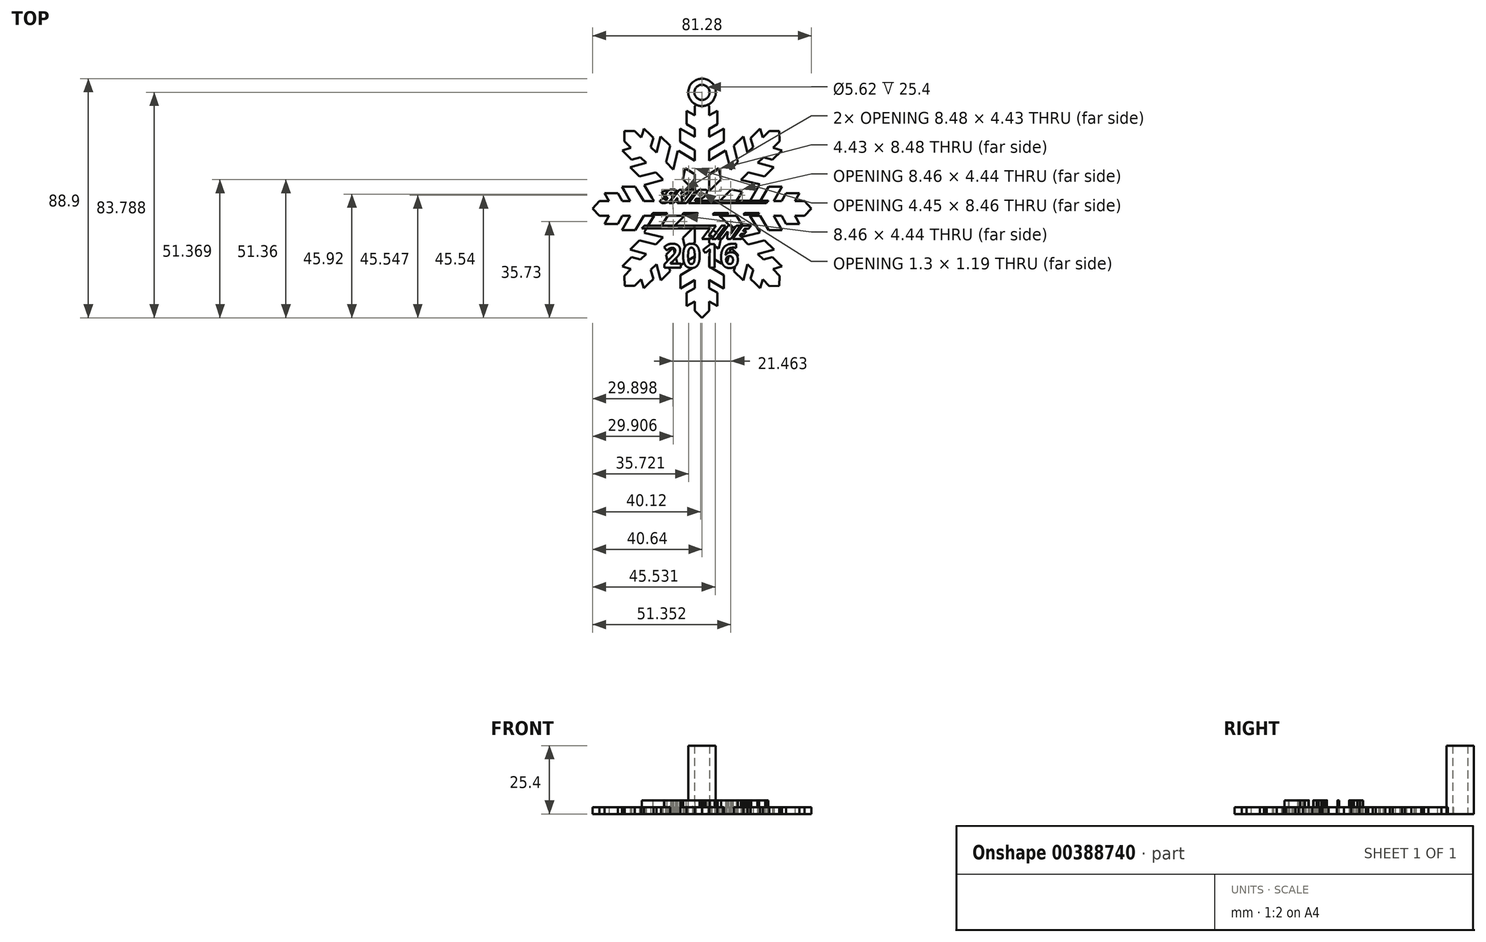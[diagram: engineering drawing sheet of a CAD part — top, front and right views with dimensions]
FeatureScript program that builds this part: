
annotation { "Feature Type Name" : "Feature", "Feature Type Description" : "" }
export const myFeature = defineFeature(function(context is Context, id is Id, definition is map)
    precondition{}
    {
        {
            var Q0;
            Q0=qCreatedBy(makeId("Top.planeOp"),FACE);
            var sketch = newSketch(context, id + "F0", { "sketchPlane" : qUnion([Q0])});
            skFitSpline(sketch, "E0", {"points": [v(-1.17, 4.88) * mm, v(-0.68, 4.68) * mm, v(0.05, 5.08) * mm, v(0.12, 5.6) * mm]});
            skArc(sketch, "E1", {"start": v(0.12, 5.6) * mm, "mid": v(0.11, 5.67) * mm, "end": v(0.07, 5.73) * mm});
            skFitSpline(sketch, "E2", {"points": [v(0.07, 5.73) * mm, v(-0.05, 5.86) * mm, v(-0.5, 5.81) * mm, v(-0.6, 5.67) * mm]});
            skLineSegment(sketch, "E3", {"start": v(-0.6, 5.67) * mm, "end": v(-1.17, 4.88) * mm});
            skEllipticalArc(sketch, "E4", {});
            skArc(sketch, "E5", {"start": v(15.96, -7.56) * mm, "mid": v(15.87, -7.56) * mm, "end": v(15.8, -7.6) * mm});
            skArc(sketch, "E6", {"start": v(15.8, -7.6) * mm, "mid": v(15.52, -7.98) * mm, "end": v(15.26, -8.37) * mm});
            skLineSegment(sketch, "E7", {"start": v(15.26, -8.37) * mm, "end": v(16.54, -8.4) * mm});
            skArc(sketch, "E8", {"start": v(14.65, -9.46) * mm, "mid": v(14.5, -9.47) * mm, "end": v(14.4, -9.57) * mm});
            skArc(sketch, "E9", {"start": v(14.06, -10.09) * mm, "mid": v(14.23, -9.83) * mm, "end": v(14.4, -9.57) * mm});
            skLineSegment(sketch, "E10", {"start": v(15.39, -10.18) * mm, "end": v(14.62, -11.34) * mm});
            skArc(sketch, "E11", {"start": v(14.5, -11.4) * mm, "mid": v(14.56, -11.38) * mm, "end": v(14.62, -11.34) * mm});
            skLineSegment(sketch, "E12", {"start": v(-9.28, 6.52) * mm, "end": v(-10.53, 5.46) * mm});
            skArc(sketch, "E13", {"start": v(-10.53, 5.46) * mm, "mid": v(-10.74, 5.59) * mm, "end": v(-10.96, 5.7) * mm});
            skArc(sketch, "E14", {"start": v(-10.96, 5.7) * mm, "mid": v(-11.16, 5.75) * mm, "end": v(-11.37, 5.75) * mm});
            skFitSpline(sketch, "E15", {"points": [v(-11.37, 5.75) * mm, v(-11.84, 5.7) * mm, v(-11.92, 5.5) * mm, v(-11.63, 5.14) * mm]});
            skArc(sketch, "E16", {"start": v(-11.63, 5.14) * mm, "mid": v(-11.41, 4.9) * mm, "end": v(-11.19, 4.67) * mm});
            skArc(sketch, "E17", {"start": v(-11.05, 4.4) * mm, "mid": v(-11.1, 4.55) * mm, "end": v(-11.19, 4.67) * mm});
            skArc(sketch, "E18", {"start": v(-11.29, 3.53) * mm, "mid": v(-11.1, 3.95) * mm, "end": v(-11.05, 4.4) * mm});
            skArc(sketch, "E19", {"start": v(-13, 2.22) * mm, "mid": v(-12.04, 2.74) * mm, "end": v(-11.29, 3.53) * mm});
            skArc(sketch, "E20", {"start": v(-14.5, 1.95) * mm, "mid": v(-13.73, 2) * mm, "end": v(-13, 2.22) * mm});
            skArc(sketch, "E21", {"start": v(-15.55, 2.56) * mm, "mid": v(-15.1, 2.13) * mm, "end": v(-14.5, 1.95) * mm});
            skArc(sketch, "E22", {"start": v(-15.5, 2.93) * mm, "mid": v(-15.61, 2.76) * mm, "end": v(-15.55, 2.56) * mm});
            skFitSpline(sketch, "E23", {"points": [v(-13.41, 5.49) * mm, v(-12.78, 6.4) * mm, v(-11.95, 6.98) * mm, v(-10.83, 7.1) * mm]});
            skArc(sketch, "E24", {"start": v(-9.59, 6.78) * mm, "mid": v(-10.18, 7.06) * mm, "end": v(-10.83, 7.1) * mm});
            skArc(sketch, "E25", {"start": v(-9.59, 6.78) * mm, "mid": v(-9.43, 6.65) * mm, "end": v(-9.28, 6.52) * mm});
            skLineSegment(sketch, "E26", {"start": v(15.87, -9.37) * mm, "end": v(16.54, -8.4) * mm});
            skLineSegment(sketch, "E27", {"start": v(14.65, -9.46) * mm, "end": v(15.7, -9.47) * mm});
            skArc(sketch, "E28", {"start": v(15.7, -9.47) * mm, "mid": v(15.8, -9.44) * mm, "end": v(15.87, -9.37) * mm});
            skLineSegment(sketch, "E29", {"start": v(15.39, -10.18) * mm, "end": v(13.99, -10.18) * mm});
            skLineSegment(sketch, "E30", {"start": v(14.06, -10.09) * mm, "end": v(13.99, -10.18) * mm});
            skFitSpline(sketch, "E31", {"points": [v(-2.46, 3.22) * mm, v(-2.3, 3.55) * mm, v(-2.05, 3.64) * mm, v(-1.68, 3.64) * mm]});
            skFitSpline(sketch, "E32", {"points": [v(-1.68, 3.64) * mm, v(-0.53, 3.63) * mm, v(0.45, 4.01) * mm, v(1.2, 4.93) * mm]});
            skFitSpline(sketch, "E33", {"points": [v(1.2, 4.93) * mm, v(1.46, 5.25) * mm, v(1.71, 5.58) * mm, v(1.8, 6) * mm]});
            skFitSpline(sketch, "E34", {"points": [v(1.8, 6) * mm, v(1.88, 6.49) * mm, v(1.65, 6.85) * mm, v(1.16, 6.88) * mm]});
            skArc(sketch, "E35", {"start": v(-18.22, -1.75) * mm, "mid": v(-18.28, -1.76) * mm, "end": v(-18.34, -1.8) * mm});
            skLineSegment(sketch, "E36", {"start": v(-18.34, -1.8) * mm, "end": v(-18.79, -2.39) * mm});
            skLineSegment(sketch, "E37", {"start": v(-18.79, -2.39) * mm, "end": v(-13.62, -2.39) * mm});
            skArc(sketch, "E38", {"start": v(-13.62, -2.39) * mm, "mid": v(-13.55, -2.38) * mm, "end": v(-13.48, -2.35) * mm});
            skArc(sketch, "E39", {"start": v(-13.48, -2.35) * mm, "mid": v(-13.2, -2.05) * mm, "end": v(-12.9, -1.75) * mm});
            skLineSegment(sketch, "E40", {"start": v(-12.9, -1.75) * mm, "end": v(-18.22, -1.75) * mm});
            skArc(sketch, "E41", {"start": v(15.93, -1.74) * mm, "mid": v(15.84, -1.75) * mm, "end": v(15.77, -1.8) * mm});
            skLineSegment(sketch, "E42", {"start": v(15.77, -1.8) * mm, "end": v(15.35, -2.38) * mm});
            skLineSegment(sketch, "E43", {"start": v(15.35, -2.38) * mm, "end": v(20.52, -2.38) * mm});
            skArc(sketch, "E44", {"start": v(20.52, -2.38) * mm, "mid": v(20.57, -2.38) * mm, "end": v(20.62, -2.36) * mm});
            skArc(sketch, "E45", {"start": v(20.62, -2.36) * mm, "mid": v(20.92, -2.05) * mm, "end": v(21.22, -1.74) * mm});
            skLineSegment(sketch, "E46", {"start": v(21.22, -1.74) * mm, "end": v(15.93, -1.74) * mm});
            skArc(sketch, "E47", {"start": v(-5.78, 2.11) * mm, "mid": v(-5.92, 2) * mm, "end": v(-6.1, 1.96) * mm});
            skArc(sketch, "E48", {"start": v(-6.1, 1.96) * mm, "mid": v(-6.72, 1.97) * mm, "end": v(-7.33, 1.97) * mm});
            skArc(sketch, "E49", {"start": v(-7.33, 1.97) * mm, "mid": v(-7.22, 2.12) * mm, "end": v(-7.11, 2.27) * mm});
            skLineSegment(sketch, "E50", {"start": v(-7.11, 2.27) * mm, "end": v(-3.68, 6.81) * mm});
            skArc(sketch, "E51", {"start": v(-3.68, 6.81) * mm, "mid": v(-3.55, 6.93) * mm, "end": v(-3.38, 6.96) * mm});
            skArc(sketch, "E52", {"start": v(-3.38, 6.96) * mm, "mid": v(-2.77, 6.95) * mm, "end": v(-2.17, 6.96) * mm});
            skLineSegment(sketch, "E53", {"start": v(-2.17, 6.96) * mm, "end": v(-3.75, 4.83) * mm});
            skLineSegment(sketch, "E54", {"start": v(-3.75, 4.83) * mm, "end": v(-5.78, 2.11) * mm});
            skArc(sketch, "E55", {"start": v(-7.82, 5.6) * mm, "mid": v(-7.35, 6.25) * mm, "end": v(-6.88, 6.9) * mm});
            skArc(sketch, "E56", {"start": v(-6.88, 6.9) * mm, "mid": v(-6.96, 6.91) * mm, "end": v(-7.05, 6.93) * mm});
            skArc(sketch, "E57", {"start": v(-7.05, 6.93) * mm, "mid": v(-7.61, 6.93) * mm, "end": v(-8.17, 6.93) * mm});
            skArc(sketch, "E58", {"start": v(-8.17, 6.93) * mm, "mid": v(-8.37, 6.9) * mm, "end": v(-8.52, 6.78) * mm});
            skLineSegment(sketch, "E59", {"start": v(-8.52, 6.78) * mm, "end": v(-11.44, 3.01) * mm});
            skArc(sketch, "E60", {"start": v(-11.44, 3.01) * mm, "mid": v(-11.82, 2.52) * mm, "end": v(-12.21, 2.03) * mm});
            skArc(sketch, "E61", {"start": v(-12.21, 2.03) * mm, "mid": v(-12.06, 2.01) * mm, "end": v(-11.9, 2) * mm});
            skArc(sketch, "E62", {"start": v(-11.9, 2) * mm, "mid": v(-11.36, 2) * mm, "end": v(-10.83, 1.99) * mm});
            skArc(sketch, "E63", {"start": v(-10.83, 1.99) * mm, "mid": v(-10.66, 2) * mm, "end": v(-10.54, 2.12) * mm});
            skLineSegment(sketch, "E64", {"start": v(-10.54, 2.12) * mm, "end": v(-9.3, 3.76) * mm});
            skArc(sketch, "E65", {"start": v(-9.3, 3.76) * mm, "mid": v(-9.26, 3.8) * mm, "end": v(-9.22, 3.84) * mm});
            skLineSegment(sketch, "E66", {"start": v(-9.22, 3.84) * mm, "end": v(-9.16, 3.83) * mm});
            skLineSegment(sketch, "E67", {"start": v(-9.16, 3.83) * mm, "end": v(-9.16, 1.97) * mm});
            skLineSegment(sketch, "E68", {"start": v(-9.16, 1.97) * mm, "end": v(-7.34, 1.97) * mm});
            skLineSegment(sketch, "E69", {"start": v(-7.34, 1.97) * mm, "end": v(-7.5, 4.24) * mm});
            skArc(sketch, "E70", {"start": v(-7.5, 4.24) * mm, "mid": v(-7.46, 4.5) * mm, "end": v(-7.27, 4.67) * mm});
            skLineSegment(sketch, "E71", {"start": v(-7.27, 4.67) * mm, "end": v(-4.03, 6.74) * mm});
            skArc(sketch, "E72", {"start": v(-4.03, 6.74) * mm, "mid": v(-3.9, 6.86) * mm, "end": v(-3.76, 6.98) * mm});
            skLineSegment(sketch, "E73", {"start": v(-3.76, 6.98) * mm, "end": v(-5.75, 6.98) * mm});
            skArc(sketch, "E74", {"start": v(-5.75, 6.98) * mm, "mid": v(-5.84, 6.96) * mm, "end": v(-5.92, 6.91) * mm});
            skLineSegment(sketch, "E75", {"start": v(-5.92, 6.91) * mm, "end": v(-6.93, 6.2) * mm});
            skLineSegment(sketch, "E76", {"start": v(-6.93, 6.2) * mm, "end": v(-7.8, 5.58) * mm});
            skArc(sketch, "E77", {"start": v(-7.8, 5.58) * mm, "mid": v(-7.82, 5.6) * mm, "end": v(-7.82, 5.6) * mm});
            skLineSegment(sketch, "E78", {"start": v(-15.5, 2.93) * mm, "end": v(-14.4, 3.86) * mm});
            skArc(sketch, "E79", {"start": v(-14.4, 3.86) * mm, "mid": v(-14.2, 3.67) * mm, "end": v(-14, 3.5) * mm});
            skArc(sketch, "E80", {"start": v(-14, 3.5) * mm, "mid": v(-13.48, 3.3) * mm, "end": v(-12.97, 3.5) * mm});
            skArc(sketch, "E81", {"start": v(-12.97, 3.5) * mm, "mid": v(-12.85, 3.68) * mm, "end": v(-12.88, 3.9) * mm});
            skArc(sketch, "E82", {"start": v(-12.88, 3.9) * mm, "mid": v(-13.13, 4.24) * mm, "end": v(-13.41, 4.55) * mm});
            skArc(sketch, "E83", {"start": v(-13.41, 4.55) * mm, "mid": v(-13.58, 4.8) * mm, "end": v(-13.58, 5.1) * mm});
            skArc(sketch, "E84", {"start": v(-13.58, 5.1) * mm, "mid": v(-13.51, 5.3) * mm, "end": v(-13.41, 5.49) * mm});
            skLineSegment(sketch, "E85", {"start": v(2.96, -11.36) * mm, "end": v(0.03, -11.36) * mm});
            skLineSegment(sketch, "E86", {"start": v(0.03, -11.36) * mm, "end": v(2.93, -7.41) * mm});
            skLineSegment(sketch, "E87", {"start": v(2.93, -7.41) * mm, "end": v(-22.35, -7.41) * mm});
            skArc(sketch, "E88", {"start": v(-22.35, -7.41) * mm, "mid": v(-21.88, -6.88) * mm, "end": v(-21.4, -6.36) * mm});
            skLineSegment(sketch, "E89", {"start": v(-21.4, -6.36) * mm, "end": v(5.26, -6.38) * mm});
            skLineSegment(sketch, "E90", {"start": v(5.26, -6.38) * mm, "end": v(2.48, -10.16) * mm});
            skArc(sketch, "E91", {"start": v(2.48, -10.16) * mm, "mid": v(3.16, -10.16) * mm, "end": v(3.85, -10.17) * mm});
            skArc(sketch, "E92", {"start": v(3.85, -10.17) * mm, "mid": v(3.47, -10.74) * mm, "end": v(3.08, -11.32) * mm});
            skArc(sketch, "E93", {"start": v(3.08, -11.32) * mm, "mid": v(3.02, -11.35) * mm, "end": v(2.96, -11.36) * mm});
            skArc(sketch, "E94", {"start": v(7.46, -6.36) * mm, "mid": v(7.32, -6.39) * mm, "end": v(7.21, -6.48) * mm});
            skLineSegment(sketch, "E95", {"start": v(7.21, -6.48) * mm, "end": v(3.73, -11.26) * mm});
            skArc(sketch, "E96", {"start": v(3.73, -11.26) * mm, "mid": v(3.69, -11.33) * mm, "end": v(3.66, -11.4) * mm});
            skLineSegment(sketch, "E97", {"start": v(3.66, -11.4) * mm, "end": v(5, -11.4) * mm});
            skArc(sketch, "E98", {"start": v(5, -11.4) * mm, "mid": v(5.1, -11.37) * mm, "end": v(5.17, -11.3) * mm});
            skArc(sketch, "E99", {"start": v(5.17, -11.3) * mm, "mid": v(5.52, -10.83) * mm, "end": v(5.87, -10.36) * mm});
            skLineSegment(sketch, "E100", {"start": v(5.87, -10.36) * mm, "end": v(8.74, -6.42) * mm});
            skLineSegment(sketch, "E101", {"start": v(8.74, -6.42) * mm, "end": v(8.73, -6.36) * mm});
            skLineSegment(sketch, "E102", {"start": v(8.73, -6.36) * mm, "end": v(7.46, -6.36) * mm});
            skLineSegment(sketch, "E103", {"start": v(10.81, -9.31) * mm, "end": v(12.68, -6.56) * mm});
            skArc(sketch, "E104", {"start": v(12.68, -6.56) * mm, "mid": v(12.84, -6.43) * mm, "end": v(13.03, -6.36) * mm});
            skArc(sketch, "E105", {"start": v(13.03, -6.36) * mm, "mid": v(13.65, -6.36) * mm, "end": v(14.26, -6.37) * mm});
            skArc(sketch, "E106", {"start": v(14.26, -6.37) * mm, "mid": v(14.2, -6.45) * mm, "end": v(14.14, -6.54) * mm});
            skLineSegment(sketch, "E107", {"start": v(14.14, -6.54) * mm, "end": v(10.76, -11.26) * mm});
            skArc(sketch, "E108", {"start": v(10.76, -11.26) * mm, "mid": v(10.64, -11.37) * mm, "end": v(10.49, -11.4) * mm});
            skArc(sketch, "E109", {"start": v(10.49, -11.4) * mm, "mid": v(9.95, -11.39) * mm, "end": v(9.4, -11.39) * mm});
            skLineSegment(sketch, "E110", {"start": v(9.4, -11.39) * mm, "end": v(9.52, -8.57) * mm});
            skLineSegment(sketch, "E111", {"start": v(9.52, -8.57) * mm, "end": v(7.54, -11.25) * mm});
            skArc(sketch, "E112", {"start": v(7.54, -11.25) * mm, "mid": v(7.4, -11.35) * mm, "end": v(7.24, -11.38) * mm});
            skArc(sketch, "E113", {"start": v(7.24, -11.38) * mm, "mid": v(6.56, -11.38) * mm, "end": v(5.89, -11.38) * mm});
            skArc(sketch, "E114", {"start": v(5.89, -11.38) * mm, "mid": v(5.96, -11.28) * mm, "end": v(6.03, -11.17) * mm});
            skLineSegment(sketch, "E115", {"start": v(6.03, -11.17) * mm, "end": v(9.6, -6.48) * mm});
            skArc(sketch, "E116", {"start": v(9.6, -6.48) * mm, "mid": v(9.74, -6.35) * mm, "end": v(9.91, -6.32) * mm});
            skArc(sketch, "E117", {"start": v(9.91, -6.32) * mm, "mid": v(10.45, -6.33) * mm, "end": v(11, -6.33) * mm});
            skLineSegment(sketch, "E118", {"start": v(11, -6.33) * mm, "end": v(10.78, -9.3) * mm});
            skLineSegment(sketch, "E119", {"start": v(14.5, -11.4) * mm, "end": v(11.59, -11.38) * mm});
            skLineSegment(sketch, "E120", {"start": v(11.59, -11.38) * mm, "end": v(11.44, -11.35) * mm});
            skLineSegment(sketch, "E121", {"start": v(11.44, -11.35) * mm, "end": v(12.5, -9.88) * mm});
            skLineSegment(sketch, "E122", {"start": v(12.5, -9.88) * mm, "end": v(14.94, -6.53) * mm});
            skArc(sketch, "E123", {"start": v(14.94, -6.53) * mm, "mid": v(15.06, -6.42) * mm, "end": v(15.21, -6.39) * mm});
            skLineSegment(sketch, "E124", {"start": v(15.21, -6.39) * mm, "end": v(18.1, -6.36) * mm});
            skArc(sketch, "E125", {"start": v(18.1, -6.36) * mm, "mid": v(18.18, -6.36) * mm, "end": v(18.26, -6.37) * mm});
            skArc(sketch, "E126", {"start": v(18.26, -6.37) * mm, "mid": v(18.1, -6.57) * mm, "end": v(17.92, -6.77) * mm});
            skArc(sketch, "E127", {"start": v(17.92, -6.77) * mm, "mid": v(17.62, -7.14) * mm, "end": v(17.31, -7.5) * mm});
            skArc(sketch, "E128", {"start": v(17.31, -7.5) * mm, "mid": v(17.2, -7.55) * mm, "end": v(17.1, -7.56) * mm});
            skArc(sketch, "E129", {"start": v(17.1, -7.56) * mm, "mid": v(16.53, -7.56) * mm, "end": v(15.96, -7.56) * mm});
            skArc(sketch, "E130", {"start": v(-2.7, 2.87) * mm, "mid": v(-2.57, 3.04) * mm, "end": v(-2.46, 3.22) * mm});
            skLineSegment(sketch, "E131", {"start": v(-2.7, 2.87) * mm, "end": v(24.62, 2.87) * mm});
            skArc(sketch, "E132", {"start": v(24.64, 2.8) * mm, "mid": v(24.38, 2.54) * mm, "end": v(24.14, 2.26) * mm});
            skArc(sketch, "E133", {"start": v(23.53, 1.99) * mm, "mid": v(23.87, 2.04) * mm, "end": v(24.14, 2.26) * mm});
            skLineSegment(sketch, "E134", {"start": v(23.53, 1.99) * mm, "end": v(6.56, 1.99) * mm});
            skLineSegment(sketch, "E135", {"start": v(6.56, 1.99) * mm, "end": v(6.54, 1.99) * mm});
            skLineSegment(sketch, "E136", {"start": v(6.54, 1.99) * mm, "end": v(-4.65, 1.98) * mm});
            skLineSegment(sketch, "E137", {"start": v(-4.65, 1.98) * mm, "end": v(-4.9, 1.98) * mm});
            skArc(sketch, "E138", {"start": v(-4.8, 2.14) * mm, "mid": v(-4.85, 2.06) * mm, "end": v(-4.9, 1.98) * mm});
            skLineSegment(sketch, "E139", {"start": v(-4.8, 2.14) * mm, "end": v(-1.22, 6.8) * mm});
            skArc(sketch, "E140", {"start": v(-0.9, 6.97) * mm, "mid": v(-1.08, 6.94) * mm, "end": v(-1.22, 6.8) * mm});
            skArc(sketch, "E141", {"start": v(1.16, 6.88) * mm, "mid": v(0.14, 6.94) * mm, "end": v(-0.9, 6.97) * mm});
            skLineSegment(sketch, "E142", {"start": v(24.64, 2.8) * mm, "end": v(24.62, 2.87) * mm});
            skLineSegment(sketch, "E143", {"start": v(-6.82, -1.75) * mm, "end": v(-1.61, -1.75) * mm});
            skArc(sketch, "E144", {"start": v(-2.1, -2.34) * mm, "mid": v(-1.83, -2.06) * mm, "end": v(-1.56, -1.78) * mm});
            skArc(sketch, "E145", {"start": v(-2.23, -2.37) * mm, "mid": v(-2.17, -2.37) * mm, "end": v(-2.1, -2.34) * mm});
            skLineSegment(sketch, "E146", {"start": v(-2.23, -2.37) * mm, "end": v(-7.43, -2.37) * mm});
            skLineSegment(sketch, "E147", {"start": v(-7.43, -2.37) * mm, "end": v(-6.98, -1.81) * mm});
            skArc(sketch, "E148", {"start": v(-6.82, -1.75) * mm, "mid": v(-6.9, -1.77) * mm, "end": v(-6.98, -1.81) * mm});
            skLineSegment(sketch, "E149", {"start": v(-1.56, -1.78) * mm, "end": v(-1.61, -1.75) * mm});
            skArc(sketch, "E150", {"start": v(4.52, -1.76) * mm, "mid": v(4.44, -1.78) * mm, "end": v(4.37, -1.82) * mm});
            skLineSegment(sketch, "E151", {"start": v(4.37, -1.82) * mm, "end": v(3.92, -2.38) * mm});
            skLineSegment(sketch, "E152", {"start": v(3.92, -2.38) * mm, "end": v(9.11, -2.38) * mm});
            skArc(sketch, "E153", {"start": v(9.11, -2.38) * mm, "mid": v(9.18, -2.38) * mm, "end": v(9.24, -2.35) * mm});
            skArc(sketch, "E154", {"start": v(9.79, -1.79) * mm, "mid": v(9.5, -2.07) * mm, "end": v(9.24, -2.35) * mm});
            skLineSegment(sketch, "E155", {"start": v(9.73, -1.76) * mm, "end": v(4.52, -1.76) * mm});
            skLineSegment(sketch, "E156", {"start": v(9.79, -1.79) * mm, "end": v(9.73, -1.76) * mm});
            const initialGuessF0  = {"E4": [0.010823041612434577, -0.009243857390442117, 0.9870975910491284, -0.16011978561379503, 6.825542101971352e-05, 6.825542101971352e-05, 4.110214, 4.709019]};
            skSetInitialGuess(sketch, initialGuessF0);
            skSolve(sketch);
        }
        {
            var Q0;
            Q0 = qSketchRegion(id + "F0", true);
            extrude(context, id + "F1", {"entities" : qUnion([Q0]), "depth" : 5.08 * mm});
        }
        {
            var Q0;
            Q0=qCreatedBy(makeId("Top.planeOp"),FACE);
            var sketch = newSketch(context, id + "F2", { "sketchPlane" : qUnion([Q0])});
            skLineSegment(sketch, "E157", {"start": v(40.64, -0.01) * mm, "end": v(40.63, 0) * mm});
            skLineSegment(sketch, "E158", {"start": v(40.63, 0) * mm, "end": v(38.05, 2.69) * mm});
            skLineSegment(sketch, "E159", {"start": v(38.05, 2.69) * mm, "end": v(34.6, 2.69) * mm});
            skLineSegment(sketch, "E160", {"start": v(34.6, 2.69) * mm, "end": v(36.21, 5.73) * mm});
            skLineSegment(sketch, "E161", {"start": v(36.21, 5.73) * mm, "end": v(31.28, 5.73) * mm});
            skLineSegment(sketch, "E162", {"start": v(31.28, 5.73) * mm, "end": v(29.58, 2.69) * mm});
            skLineSegment(sketch, "E163", {"start": v(29.58, 2.69) * mm, "end": v(26.63, 2.69) * mm});
            skLineSegment(sketch, "E164", {"start": v(26.63, 2.69) * mm, "end": v(29.72, 8.08) * mm});
            skLineSegment(sketch, "E165", {"start": v(29.72, 8.08) * mm, "end": v(24.8, 8.08) * mm});
            skLineSegment(sketch, "E166", {"start": v(24.8, 8.08) * mm, "end": v(21.6, 2.69) * mm});
            skLineSegment(sketch, "E167", {"start": v(21.6, 2.69) * mm, "end": v(17.77, 2.69) * mm});
            skLineSegment(sketch, "E168", {"start": v(17.77, 2.69) * mm, "end": v(20.93, 8.17) * mm});
            skLineSegment(sketch, "E169", {"start": v(20.93, 8.17) * mm, "end": v(21.42, 9.02) * mm});
            skLineSegment(sketch, "E170", {"start": v(21.42, 9.02) * mm, "end": v(14.47, 10.68) * mm});
            skLineSegment(sketch, "E171", {"start": v(14.47, 10.68) * mm, "end": v(16.73, 12.94) * mm});
            skLineSegment(sketch, "E172", {"start": v(16.73, 12.94) * mm, "end": v(17.18, 13.39) * mm});
            skLineSegment(sketch, "E173", {"start": v(17.18, 13.39) * mm, "end": v(23.25, 11.84) * mm});
            skLineSegment(sketch, "E174", {"start": v(23.25, 11.84) * mm, "end": v(26.72, 15.32) * mm});
            skLineSegment(sketch, "E175", {"start": v(26.72, 15.32) * mm, "end": v(20.73, 16.95) * mm});
            skLineSegment(sketch, "E176", {"start": v(20.73, 16.95) * mm, "end": v(22.81, 19.03) * mm});
            skLineSegment(sketch, "E177", {"start": v(22.81, 19.03) * mm, "end": v(26.18, 18.08) * mm});
            skLineSegment(sketch, "E178", {"start": v(26.18, 18.08) * mm, "end": v(29.66, 21.56) * mm});
            skLineSegment(sketch, "E179", {"start": v(29.66, 21.56) * mm, "end": v(26.36, 22.56) * mm});
            skLineSegment(sketch, "E180", {"start": v(26.36, 22.56) * mm, "end": v(28.8, 25) * mm});
            skLineSegment(sketch, "E181", {"start": v(28.8, 25) * mm, "end": v(28.73, 28.74) * mm});
            skLineSegment(sketch, "E182", {"start": v(28.73, 28.74) * mm, "end": v(25, 28.8) * mm});
            skLineSegment(sketch, "E183", {"start": v(25, 28.8) * mm, "end": v(22.56, 26.36) * mm});
            skLineSegment(sketch, "E184", {"start": v(22.56, 26.36) * mm, "end": v(21.55, 29.66) * mm});
            skLineSegment(sketch, "E185", {"start": v(21.55, 29.66) * mm, "end": v(18.07, 26.18) * mm});
            skLineSegment(sketch, "E186", {"start": v(18.07, 26.18) * mm, "end": v(19.02, 22.82) * mm});
            skLineSegment(sketch, "E187", {"start": v(19.02, 22.82) * mm, "end": v(16.93, 20.74) * mm});
            skLineSegment(sketch, "E188", {"start": v(16.93, 20.74) * mm, "end": v(15.3, 26.74) * mm});
            skLineSegment(sketch, "E189", {"start": v(15.3, 26.74) * mm, "end": v(11.83, 23.26) * mm});
            skLineSegment(sketch, "E190", {"start": v(11.83, 23.26) * mm, "end": v(13.38, 17.19) * mm});
            skLineSegment(sketch, "E191", {"start": v(13.38, 17.19) * mm, "end": v(10.67, 14.47) * mm});
            skLineSegment(sketch, "E192", {"start": v(10.67, 14.47) * mm, "end": v(8.78, 21.53) * mm});
            skLineSegment(sketch, "E193", {"start": v(8.78, 21.53) * mm, "end": v(3.94, 18.56) * mm});
            skLineSegment(sketch, "E194", {"start": v(3.94, 18.56) * mm, "end": v(2.68, 17.8) * mm});
            skLineSegment(sketch, "E195", {"start": v(2.68, 17.8) * mm, "end": v(2.68, 21.62) * mm});
            skLineSegment(sketch, "E196", {"start": v(2.68, 21.62) * mm, "end": v(8.07, 24.82) * mm});
            skLineSegment(sketch, "E197", {"start": v(8.07, 24.82) * mm, "end": v(8.07, 29.74) * mm});
            skLineSegment(sketch, "E198", {"start": v(8.07, 29.74) * mm, "end": v(2.68, 26.64) * mm});
            skLineSegment(sketch, "E199", {"start": v(2.68, 26.64) * mm, "end": v(2.68, 29.6) * mm});
            skLineSegment(sketch, "E200", {"start": v(2.68, 29.6) * mm, "end": v(5.72, 31.3) * mm});
            skLineSegment(sketch, "E201", {"start": v(5.72, 31.3) * mm, "end": v(5.72, 36.22) * mm});
            skLineSegment(sketch, "E202", {"start": v(5.72, 36.22) * mm, "end": v(2.68, 34.6) * mm});
            skLineSegment(sketch, "E203", {"start": v(2.68, 34.6) * mm, "end": v(2.68, 38.05) * mm});
            skLineSegment(sketch, "E204", {"start": v(2.68, 38.05) * mm, "end": v(0, 40.64) * mm});
            skLineSegment(sketch, "E205", {"start": v(0, 40.64) * mm, "end": v(-2.69, 38.05) * mm});
            skLineSegment(sketch, "E206", {"start": v(-2.69, 38.05) * mm, "end": v(-2.69, 34.6) * mm});
            skLineSegment(sketch, "E207", {"start": v(-2.69, 34.6) * mm, "end": v(-5.73, 36.22) * mm});
            skLineSegment(sketch, "E208", {"start": v(-5.73, 36.22) * mm, "end": v(-5.73, 34.8) * mm});
            skLineSegment(sketch, "E209", {"start": v(-5.73, 34.8) * mm, "end": v(-5.73, 31.3) * mm});
            skLineSegment(sketch, "E210", {"start": v(-5.73, 31.3) * mm, "end": v(-2.69, 29.6) * mm});
            skLineSegment(sketch, "E211", {"start": v(-2.69, 29.6) * mm, "end": v(-2.69, 26.64) * mm});
            skLineSegment(sketch, "E212", {"start": v(-2.69, 26.64) * mm, "end": v(-8.08, 29.74) * mm});
            skLineSegment(sketch, "E213", {"start": v(-8.08, 29.74) * mm, "end": v(-8.08, 24.82) * mm});
            skLineSegment(sketch, "E214", {"start": v(-8.08, 24.82) * mm, "end": v(-4.29, 22.57) * mm});
            skLineSegment(sketch, "E215", {"start": v(-4.29, 22.57) * mm, "end": v(-2.68, 21.62) * mm});
            skLineSegment(sketch, "E216", {"start": v(-2.68, 21.62) * mm, "end": v(-2.68, 17.78) * mm});
            skLineSegment(sketch, "E217", {"start": v(-2.68, 17.78) * mm, "end": v(-8.62, 21.37) * mm});
            skLineSegment(sketch, "E218", {"start": v(-8.62, 21.37) * mm, "end": v(-8.66, 21.22) * mm});
            skLineSegment(sketch, "E219", {"start": v(-8.66, 21.22) * mm, "end": v(-9.01, 21.43) * mm});
            skLineSegment(sketch, "E220", {"start": v(-9.01, 21.43) * mm, "end": v(-10.68, 14.48) * mm});
            skLineSegment(sketch, "E221", {"start": v(-10.68, 14.48) * mm, "end": v(-10.68, 14.48) * mm});
            skLineSegment(sketch, "E222", {"start": v(-10.68, 14.48) * mm, "end": v(-13.39, 17.2) * mm});
            skLineSegment(sketch, "E223", {"start": v(-13.39, 17.2) * mm, "end": v(-11.84, 23.26) * mm});
            skLineSegment(sketch, "E224", {"start": v(-11.84, 23.26) * mm, "end": v(-15.31, 26.74) * mm});
            skLineSegment(sketch, "E225", {"start": v(-15.31, 26.74) * mm, "end": v(-16.94, 20.74) * mm});
            skLineSegment(sketch, "E226", {"start": v(-16.94, 20.74) * mm, "end": v(-19.02, 22.82) * mm});
            skLineSegment(sketch, "E227", {"start": v(-19.02, 22.82) * mm, "end": v(-18.08, 26.18) * mm});
            skLineSegment(sketch, "E228", {"start": v(-18.08, 26.18) * mm, "end": v(-19.24, 27.34) * mm});
            skLineSegment(sketch, "E229", {"start": v(-19.24, 27.34) * mm, "end": v(-21.56, 29.66) * mm});
            skLineSegment(sketch, "E230", {"start": v(-21.56, 29.66) * mm, "end": v(-22.04, 28.1) * mm});
            skLineSegment(sketch, "E231", {"start": v(-22.04, 28.1) * mm, "end": v(-22.56, 26.36) * mm});
            skLineSegment(sketch, "E232", {"start": v(-22.56, 26.36) * mm, "end": v(-25.01, 28.8) * mm});
            skLineSegment(sketch, "E233", {"start": v(-25.01, 28.8) * mm, "end": v(-28.78, 28.73) * mm});
            skLineSegment(sketch, "E234", {"start": v(-28.78, 28.73) * mm, "end": v(-28.8, 25.9) * mm});
            skLineSegment(sketch, "E235", {"start": v(-28.8, 25.9) * mm, "end": v(-28.8, 25) * mm});
            skLineSegment(sketch, "E236", {"start": v(-28.8, 25) * mm, "end": v(-26.37, 22.56) * mm});
            skLineSegment(sketch, "E237", {"start": v(-26.37, 22.56) * mm, "end": v(-29.66, 21.56) * mm});
            skLineSegment(sketch, "E238", {"start": v(-29.66, 21.56) * mm, "end": v(-26.18, 18.08) * mm});
            skLineSegment(sketch, "E239", {"start": v(-26.18, 18.08) * mm, "end": v(-22.83, 19.02) * mm});
            skLineSegment(sketch, "E240", {"start": v(-22.83, 19.02) * mm, "end": v(-20.74, 16.94) * mm});
            skLineSegment(sketch, "E241", {"start": v(-20.74, 16.94) * mm, "end": v(-26.74, 15.31) * mm});
            skLineSegment(sketch, "E242", {"start": v(-26.74, 15.31) * mm, "end": v(-25.87, 14.45) * mm});
            skLineSegment(sketch, "E243", {"start": v(-25.87, 14.45) * mm, "end": v(-23.26, 11.84) * mm});
            skLineSegment(sketch, "E244", {"start": v(-23.26, 11.84) * mm, "end": v(-17.18, 13.38) * mm});
            skLineSegment(sketch, "E245", {"start": v(-17.18, 13.38) * mm, "end": v(-15.01, 11.22) * mm});
            skLineSegment(sketch, "E246", {"start": v(-15.01, 11.22) * mm, "end": v(-14.47, 10.67) * mm});
            skLineSegment(sketch, "E247", {"start": v(-14.47, 10.67) * mm, "end": v(-21.53, 8.78) * mm});
            skLineSegment(sketch, "E248", {"start": v(-21.53, 8.78) * mm, "end": v(-18.53, 3.89) * mm});
            skLineSegment(sketch, "E249", {"start": v(-18.53, 3.89) * mm, "end": v(-17.8, 2.69) * mm});
            skLineSegment(sketch, "E250", {"start": v(-17.8, 2.69) * mm, "end": v(-20.34, 2.69) * mm});
            skLineSegment(sketch, "E251", {"start": v(-20.34, 2.69) * mm, "end": v(-21.62, 2.69) * mm});
            skLineSegment(sketch, "E252", {"start": v(-21.62, 2.69) * mm, "end": v(-24.24, 7.12) * mm});
            skLineSegment(sketch, "E253", {"start": v(-24.24, 7.12) * mm, "end": v(-24.81, 8.08) * mm});
            skLineSegment(sketch, "E254", {"start": v(-24.81, 8.08) * mm, "end": v(-29.73, 8.08) * mm});
            skLineSegment(sketch, "E255", {"start": v(-29.73, 8.08) * mm, "end": v(-28.86, 6.57) * mm});
            skLineSegment(sketch, "E256", {"start": v(-28.86, 6.57) * mm, "end": v(-26.64, 2.7) * mm});
            skLineSegment(sketch, "E257", {"start": v(-26.64, 2.7) * mm, "end": v(-29.59, 2.7) * mm});
            skLineSegment(sketch, "E258", {"start": v(-29.59, 2.7) * mm, "end": v(-31.3, 5.73) * mm});
            skLineSegment(sketch, "E259", {"start": v(-31.3, 5.73) * mm, "end": v(-36.2, 5.73) * mm});
            skLineSegment(sketch, "E260", {"start": v(-36.2, 5.73) * mm, "end": v(-34.6, 2.7) * mm});
            skLineSegment(sketch, "E261", {"start": v(-34.6, 2.7) * mm, "end": v(-38.05, 2.7) * mm});
            skLineSegment(sketch, "E262", {"start": v(-38.05, 2.7) * mm, "end": v(-40.64, 0) * mm});
            skLineSegment(sketch, "E263", {"start": v(-40.64, 0) * mm, "end": v(-38.05, -2.69) * mm});
            skLineSegment(sketch, "E264", {"start": v(-38.05, -2.69) * mm, "end": v(-34.6, -2.69) * mm});
            skLineSegment(sketch, "E265", {"start": v(-34.6, -2.69) * mm, "end": v(-36.2, -5.72) * mm});
            skLineSegment(sketch, "E266", {"start": v(-36.2, -5.72) * mm, "end": v(-35.5, -5.72) * mm});
            skLineSegment(sketch, "E267", {"start": v(-35.5, -5.72) * mm, "end": v(-31.3, -5.72) * mm});
            skLineSegment(sketch, "E268", {"start": v(-31.3, -5.72) * mm, "end": v(-29.59, -2.69) * mm});
            skLineSegment(sketch, "E269", {"start": v(-29.59, -2.69) * mm, "end": v(-26.64, -2.69) * mm});
            skLineSegment(sketch, "E270", {"start": v(-26.64, -2.69) * mm, "end": v(-29.73, -8.07) * mm});
            skLineSegment(sketch, "E271", {"start": v(-29.73, -8.07) * mm, "end": v(-24.81, -8.07) * mm});
            skLineSegment(sketch, "E272", {"start": v(-24.81, -8.07) * mm, "end": v(-21.62, -2.69) * mm});
            skLineSegment(sketch, "E273", {"start": v(-21.62, -2.69) * mm, "end": v(-17.78, -2.69) * mm});
            skLineSegment(sketch, "E274", {"start": v(-17.78, -2.69) * mm, "end": v(-21.37, -8.6) * mm});
            skLineSegment(sketch, "E275", {"start": v(-21.37, -8.6) * mm, "end": v(-21.22, -8.66) * mm});
            skLineSegment(sketch, "E276", {"start": v(-21.22, -8.66) * mm, "end": v(-21.43, -9.01) * mm});
            skLineSegment(sketch, "E277", {"start": v(-21.43, -9.01) * mm, "end": v(-14.48, -10.68) * mm});
            skLineSegment(sketch, "E278", {"start": v(-14.48, -10.68) * mm, "end": v(-17.18, -13.39) * mm});
            skLineSegment(sketch, "E279", {"start": v(-17.18, -13.39) * mm, "end": v(-23.26, -11.84) * mm});
            skLineSegment(sketch, "E280", {"start": v(-23.26, -11.84) * mm, "end": v(-26.73, -15.3) * mm});
            skLineSegment(sketch, "E281", {"start": v(-26.73, -15.3) * mm, "end": v(-20.74, -16.94) * mm});
            skLineSegment(sketch, "E282", {"start": v(-20.74, -16.94) * mm, "end": v(-22.82, -19.02) * mm});
            skLineSegment(sketch, "E283", {"start": v(-22.82, -19.02) * mm, "end": v(-26.18, -18.08) * mm});
            skLineSegment(sketch, "E284", {"start": v(-26.18, -18.08) * mm, "end": v(-29.66, -21.56) * mm});
            skLineSegment(sketch, "E285", {"start": v(-29.66, -21.56) * mm, "end": v(-26.36, -22.56) * mm});
            skLineSegment(sketch, "E286", {"start": v(-26.36, -22.56) * mm, "end": v(-28.8, -25) * mm});
            skLineSegment(sketch, "E287", {"start": v(-28.8, -25) * mm, "end": v(-28.74, -28.74) * mm});
            skLineSegment(sketch, "E288", {"start": v(-28.74, -28.74) * mm, "end": v(-25.02, -28.8) * mm});
            skLineSegment(sketch, "E289", {"start": v(-25.02, -28.8) * mm, "end": v(-25.01, -28.8) * mm});
            skLineSegment(sketch, "E290", {"start": v(-25.01, -28.8) * mm, "end": v(-22.56, -26.36) * mm});
            skLineSegment(sketch, "E291", {"start": v(-22.56, -26.36) * mm, "end": v(-21.55, -29.66) * mm});
            skLineSegment(sketch, "E292", {"start": v(-21.55, -29.66) * mm, "end": v(-19.82, -27.92) * mm});
            skLineSegment(sketch, "E293", {"start": v(-19.82, -27.92) * mm, "end": v(-18.08, -26.18) * mm});
            skLineSegment(sketch, "E294", {"start": v(-18.08, -26.18) * mm, "end": v(-19.02, -22.82) * mm});
            skLineSegment(sketch, "E295", {"start": v(-19.02, -22.82) * mm, "end": v(-16.93, -20.74) * mm});
            skLineSegment(sketch, "E296", {"start": v(-16.93, -20.74) * mm, "end": v(-15.63, -25.55) * mm});
            skLineSegment(sketch, "E297", {"start": v(-15.63, -25.55) * mm, "end": v(-15.31, -26.74) * mm});
            skLineSegment(sketch, "E298", {"start": v(-15.31, -26.74) * mm, "end": v(-11.83, -23.25) * mm});
            skLineSegment(sketch, "E299", {"start": v(-11.83, -23.25) * mm, "end": v(-13.38, -17.18) * mm});
            skLineSegment(sketch, "E300", {"start": v(-13.38, -17.18) * mm, "end": v(-10.67, -14.46) * mm});
            skLineSegment(sketch, "E301", {"start": v(-10.67, -14.46) * mm, "end": v(-9.01, -21.2) * mm});
            skLineSegment(sketch, "E302", {"start": v(-9.01, -21.2) * mm, "end": v(-8.89, -21.12) * mm});
            skLineSegment(sketch, "E303", {"start": v(-8.89, -21.12) * mm, "end": v(-8.77, -21.52) * mm});
            skLineSegment(sketch, "E304", {"start": v(-8.77, -21.52) * mm, "end": v(-2.69, -17.8) * mm});
            skLineSegment(sketch, "E305", {"start": v(-2.69, -17.8) * mm, "end": v(-2.68, -17.79) * mm});
            skLineSegment(sketch, "E306", {"start": v(-2.68, -17.79) * mm, "end": v(-2.68, -21.61) * mm});
            skLineSegment(sketch, "E307", {"start": v(-2.68, -21.61) * mm, "end": v(-8.07, -24.82) * mm});
            skLineSegment(sketch, "E308", {"start": v(-8.07, -24.82) * mm, "end": v(-8.07, -29.73) * mm});
            skLineSegment(sketch, "E309", {"start": v(-8.07, -29.73) * mm, "end": v(-2.68, -26.64) * mm});
            skLineSegment(sketch, "E310", {"start": v(-2.68, -26.64) * mm, "end": v(-2.68, -29.6) * mm});
            skLineSegment(sketch, "E311", {"start": v(-2.68, -29.6) * mm, "end": v(-5.73, -31.3) * mm});
            skLineSegment(sketch, "E312", {"start": v(-5.73, -31.3) * mm, "end": v(-5.73, -36.22) * mm});
            skLineSegment(sketch, "E313", {"start": v(-5.73, -36.22) * mm, "end": v(-2.68, -34.6) * mm});
            skLineSegment(sketch, "E314", {"start": v(-2.68, -34.6) * mm, "end": v(-2.68, -38.05) * mm});
            skLineSegment(sketch, "E315", {"start": v(-2.68, -38.05) * mm, "end": v(0, -40.64) * mm});
            skLineSegment(sketch, "E316", {"start": v(0, -40.64) * mm, "end": v(2.69, -38.05) * mm});
            skLineSegment(sketch, "E317", {"start": v(2.69, -38.05) * mm, "end": v(2.69, -34.6) * mm});
            skLineSegment(sketch, "E318", {"start": v(2.69, -34.6) * mm, "end": v(5.73, -36.22) * mm});
            skLineSegment(sketch, "E319", {"start": v(5.73, -36.22) * mm, "end": v(5.73, -31.3) * mm});
            skLineSegment(sketch, "E320", {"start": v(5.73, -31.3) * mm, "end": v(2.69, -29.6) * mm});
            skLineSegment(sketch, "E321", {"start": v(2.69, -29.6) * mm, "end": v(2.69, -28.6) * mm});
            skLineSegment(sketch, "E322", {"start": v(2.69, -28.6) * mm, "end": v(2.69, -26.64) * mm});
            skLineSegment(sketch, "E323", {"start": v(2.69, -26.64) * mm, "end": v(7.9, -29.62) * mm});
            skLineSegment(sketch, "E324", {"start": v(7.9, -29.62) * mm, "end": v(8.08, -29.74) * mm});
            skLineSegment(sketch, "E325", {"start": v(8.08, -29.74) * mm, "end": v(8.08, -24.82) * mm});
            skLineSegment(sketch, "E326", {"start": v(8.08, -24.82) * mm, "end": v(2.69, -21.62) * mm});
            skLineSegment(sketch, "E327", {"start": v(2.69, -21.62) * mm, "end": v(2.69, -20.77) * mm});
            skLineSegment(sketch, "E328", {"start": v(2.69, -20.77) * mm, "end": v(2.69, -17.78) * mm});
            skLineSegment(sketch, "E329", {"start": v(2.69, -17.78) * mm, "end": v(7.06, -20.3) * mm});
            skLineSegment(sketch, "E330", {"start": v(7.06, -20.3) * mm, "end": v(9.02, -21.44) * mm});
            skLineSegment(sketch, "E331", {"start": v(9.02, -21.44) * mm, "end": v(10.35, -15.88) * mm});
            skLineSegment(sketch, "E332", {"start": v(10.35, -15.88) * mm, "end": v(10.68, -14.48) * mm});
            skLineSegment(sketch, "E333", {"start": v(10.68, -14.48) * mm, "end": v(13.39, -17.19) * mm});
            skLineSegment(sketch, "E334", {"start": v(13.39, -17.19) * mm, "end": v(11.84, -23.25) * mm});
            skLineSegment(sketch, "E335", {"start": v(11.84, -23.25) * mm, "end": v(15.31, -26.74) * mm});
            skLineSegment(sketch, "E336", {"start": v(15.31, -26.74) * mm, "end": v(16.94, -20.74) * mm});
            skLineSegment(sketch, "E337", {"start": v(16.94, -20.74) * mm, "end": v(18.33, -22.13) * mm});
            skLineSegment(sketch, "E338", {"start": v(18.33, -22.13) * mm, "end": v(19.02, -22.82) * mm});
            skLineSegment(sketch, "E339", {"start": v(19.02, -22.82) * mm, "end": v(18.08, -26.18) * mm});
            skLineSegment(sketch, "E340", {"start": v(18.08, -26.18) * mm, "end": v(19.81, -27.92) * mm});
            skLineSegment(sketch, "E341", {"start": v(19.81, -27.92) * mm, "end": v(21.56, -29.66) * mm});
            skLineSegment(sketch, "E342", {"start": v(21.56, -29.66) * mm, "end": v(22.56, -26.37) * mm});
            skLineSegment(sketch, "E343", {"start": v(22.56, -26.37) * mm, "end": v(25, -28.81) * mm});
            skLineSegment(sketch, "E344", {"start": v(25, -28.81) * mm, "end": v(28.74, -28.74) * mm});
            skLineSegment(sketch, "E345", {"start": v(28.74, -28.74) * mm, "end": v(28.8, -25) * mm});
            skLineSegment(sketch, "E346", {"start": v(28.8, -25) * mm, "end": v(26.37, -22.56) * mm});
            skLineSegment(sketch, "E347", {"start": v(26.37, -22.56) * mm, "end": v(29.66, -21.56) * mm});
            skLineSegment(sketch, "E348", {"start": v(29.66, -21.56) * mm, "end": v(28.62, -20.52) * mm});
            skLineSegment(sketch, "E349", {"start": v(28.62, -20.52) * mm, "end": v(26.18, -18.08) * mm});
            skLineSegment(sketch, "E350", {"start": v(26.18, -18.08) * mm, "end": v(22.82, -19.03) * mm});
            skLineSegment(sketch, "E351", {"start": v(22.82, -19.03) * mm, "end": v(20.74, -16.94) * mm});
            skLineSegment(sketch, "E352", {"start": v(20.74, -16.94) * mm, "end": v(26.73, -15.32) * mm});
            skLineSegment(sketch, "E353", {"start": v(26.73, -15.32) * mm, "end": v(23.26, -11.85) * mm});
            skLineSegment(sketch, "E354", {"start": v(23.26, -11.85) * mm, "end": v(18.28, -13.1) * mm});
            skLineSegment(sketch, "E355", {"start": v(18.28, -13.1) * mm, "end": v(17.18, -13.39) * mm});
            skLineSegment(sketch, "E356", {"start": v(17.18, -13.39) * mm, "end": v(14.47, -10.67) * mm});
            skLineSegment(sketch, "E357", {"start": v(14.47, -10.67) * mm, "end": v(21.2, -9.01) * mm});
            skLineSegment(sketch, "E358", {"start": v(21.2, -9.01) * mm, "end": v(21.13, -8.89) * mm});
            skLineSegment(sketch, "E359", {"start": v(21.13, -8.89) * mm, "end": v(21.53, -8.78) * mm});
            skLineSegment(sketch, "E360", {"start": v(21.53, -8.78) * mm, "end": v(17.79, -2.7) * mm});
            skLineSegment(sketch, "E361", {"start": v(17.79, -2.7) * mm, "end": v(21.62, -2.7) * mm});
            skLineSegment(sketch, "E362", {"start": v(21.62, -2.7) * mm, "end": v(24.4, -7.39) * mm});
            skLineSegment(sketch, "E363", {"start": v(24.4, -7.39) * mm, "end": v(24.81, -8.08) * mm});
            skLineSegment(sketch, "E364", {"start": v(24.81, -8.08) * mm, "end": v(29.73, -8.08) * mm});
            skLineSegment(sketch, "E365", {"start": v(29.73, -8.08) * mm, "end": v(27.3, -3.85) * mm});
            skLineSegment(sketch, "E366", {"start": v(27.3, -3.85) * mm, "end": v(26.64, -2.7) * mm});
            skLineSegment(sketch, "E367", {"start": v(26.64, -2.7) * mm, "end": v(29.59, -2.7) * mm});
            skLineSegment(sketch, "E368", {"start": v(29.59, -2.7) * mm, "end": v(31.3, -5.73) * mm});
            skLineSegment(sketch, "E369", {"start": v(31.3, -5.73) * mm, "end": v(33.75, -5.73) * mm});
            skLineSegment(sketch, "E370", {"start": v(33.75, -5.73) * mm, "end": v(36.22, -5.73) * mm});
            skLineSegment(sketch, "E371", {"start": v(36.22, -5.73) * mm, "end": v(35.07, -3.59) * mm});
            skLineSegment(sketch, "E372", {"start": v(35.07, -3.59) * mm, "end": v(34.6, -2.7) * mm});
            skLineSegment(sketch, "E373", {"start": v(34.6, -2.7) * mm, "end": v(38.05, -2.7) * mm});
            skLineSegment(sketch, "E374", {"start": v(38.05, -2.7) * mm, "end": v(40.64, -0.01) * mm});
            skLineSegment(sketch, "E375", {"start": v(10.9, -7.12) * mm, "end": v(7.96, -4.16) * mm});
            skLineSegment(sketch, "E376", {"start": v(7.96, -4.16) * mm, "end": v(6.48, -2.7) * mm});
            skLineSegment(sketch, "E377", {"start": v(6.48, -2.7) * mm, "end": v(12.76, -2.7) * mm});
            skLineSegment(sketch, "E378", {"start": v(12.76, -2.7) * mm, "end": v(14.07, -4.76) * mm});
            skLineSegment(sketch, "E379", {"start": v(14.07, -4.76) * mm, "end": v(14.96, -6.18) * mm});
            skLineSegment(sketch, "E380", {"start": v(14.96, -6.18) * mm, "end": v(10.9, -7.12) * mm});
            skLineSegment(sketch, "E381", {"start": v(6.17, 14.97) * mm, "end": v(7.1, 10.92) * mm});
            skLineSegment(sketch, "E382", {"start": v(7.1, 10.92) * mm, "end": v(2.67, 6.49) * mm});
            skLineSegment(sketch, "E383", {"start": v(2.67, 6.49) * mm, "end": v(2.67, 12.77) * mm});
            skLineSegment(sketch, "E384", {"start": v(2.67, 12.77) * mm, "end": v(6.17, 14.97) * mm});
            skLineSegment(sketch, "E385", {"start": v(14.94, 6.22) * mm, "end": v(12.74, 2.69) * mm});
            skLineSegment(sketch, "E386", {"start": v(12.74, 2.69) * mm, "end": v(6.48, 2.69) * mm});
            skLineSegment(sketch, "E387", {"start": v(6.48, 2.69) * mm, "end": v(10.91, 7.13) * mm});
            skLineSegment(sketch, "E388", {"start": v(10.91, 7.13) * mm, "end": v(14.52, 6.31) * mm});
            skLineSegment(sketch, "E389", {"start": v(14.52, 6.31) * mm, "end": v(14.94, 6.22) * mm});
            skLineSegment(sketch, "E390", {"start": v(2.67, -12.75) * mm, "end": v(2.67, -6.48) * mm});
            skLineSegment(sketch, "E391", {"start": v(2.67, -6.48) * mm, "end": v(7.12, -10.93) * mm});
            skLineSegment(sketch, "E392", {"start": v(7.12, -10.93) * mm, "end": v(6.2, -14.95) * mm});
            skLineSegment(sketch, "E393", {"start": v(6.2, -14.95) * mm, "end": v(2.67, -12.75) * mm});
            skLineSegment(sketch, "E394", {"start": v(-2.7, 12.76) * mm, "end": v(-2.7, 6.49) * mm});
            skLineSegment(sketch, "E395", {"start": v(-2.7, 6.49) * mm, "end": v(-7.14, 10.93) * mm});
            skLineSegment(sketch, "E396", {"start": v(-7.14, 10.93) * mm, "end": v(-6.23, 14.95) * mm});
            skLineSegment(sketch, "E397", {"start": v(-6.23, 14.95) * mm, "end": v(-3.15, 13.03) * mm});
            skLineSegment(sketch, "E398", {"start": v(-3.15, 13.03) * mm, "end": v(-2.7, 12.76) * mm});
            skLineSegment(sketch, "E399", {"start": v(-12.77, -2.7) * mm, "end": v(-6.5, -2.7) * mm});
            skLineSegment(sketch, "E400", {"start": v(-6.5, -2.7) * mm, "end": v(-10.94, -7.13) * mm});
            skLineSegment(sketch, "E401", {"start": v(-10.94, -7.13) * mm, "end": v(-14.96, -6.21) * mm});
            skLineSegment(sketch, "E402", {"start": v(-14.96, -6.21) * mm, "end": v(-12.77, -2.7) * mm});
            skLineSegment(sketch, "E403", {"start": v(-14.98, 6.18) * mm, "end": v(-10.93, 7.12) * mm});
            skLineSegment(sketch, "E404", {"start": v(-10.93, 7.12) * mm, "end": v(-6.5, 2.68) * mm});
            skLineSegment(sketch, "E405", {"start": v(-6.5, 2.68) * mm, "end": v(-12.77, 2.68) * mm});
            skLineSegment(sketch, "E406", {"start": v(-12.77, 2.68) * mm, "end": v(-14.84, 5.95) * mm});
            skLineSegment(sketch, "E407", {"start": v(-14.84, 5.95) * mm, "end": v(-14.98, 6.18) * mm});
            skLineSegment(sketch, "E408", {"start": v(-7.13, -10.92) * mm, "end": v(-2.7, -6.48) * mm});
            skLineSegment(sketch, "E409", {"start": v(-2.7, -6.48) * mm, "end": v(-2.7, -12.76) * mm});
            skLineSegment(sketch, "E410", {"start": v(-2.7, -12.76) * mm, "end": v(-6.2, -14.97) * mm});
            skLineSegment(sketch, "E411", {"start": v(-6.2, -14.97) * mm, "end": v(-6.87, -12.07) * mm});
            skLineSegment(sketch, "E412", {"start": v(-6.87, -12.07) * mm, "end": v(-7.13, -10.92) * mm});
            skSolve(sketch);
        }
        {
            var Q0;
            Q0 = qSketchRegion(id + "F2", true);
            extrude(context, id + "F3", {"entities" : qUnion([Q0]), "depth" : 2.54 * mm});
        }
        {
            var Q0;
            Q0=qCreatedBy(makeId("Top.planeOp"),FACE);
            var sketch = newSketch(context, id + "F4", { "sketchPlane" : qUnion([Q0])});
            skText(sketch, "E413", { "text": "2016", "fontName": "OpenSans-Bold.ttf"});
            const initialGuessF4  = {"E413": [-0.01452, -0.02203, 1, 0, 0.0089]};
            skSetInitialGuess(sketch, initialGuessF4);
            skSolve(sketch);
        }
        {
            var Q0;
            Q0 = qSketchRegion(id + "F4", true);
            extrude(context, id + "F5", {"entities" : qUnion([Q0]), "operationType" : NewBodyOperationType.ADD, "depth" : 5.08 * mm});
        }
        {
            var Q0;
            Q0=qCreatedBy(makeId("Top.planeOp"),FACE);
            var sketch = newSketch(context, id + "F6", { "sketchPlane" : qUnion([Q0])});
            skCircle(sketch, "E414", {"center": v(0, 43.15) * mm, "radius": 5.1 * mm});
            skCircle(sketch, "E415", {"center": v(0, 43.15) * mm, "radius": 2.81 * mm});
            skSolve(sketch);
        }
        {
            var Q0;
            Q0 = qSketchRegion(id + "F6", true);
            extrude(context, id + "F7", {"entities" : qUnion([Q0]), "operationType" : NewBodyOperationType.ADD, "depth" : 25.4 * mm});
        }
    });
